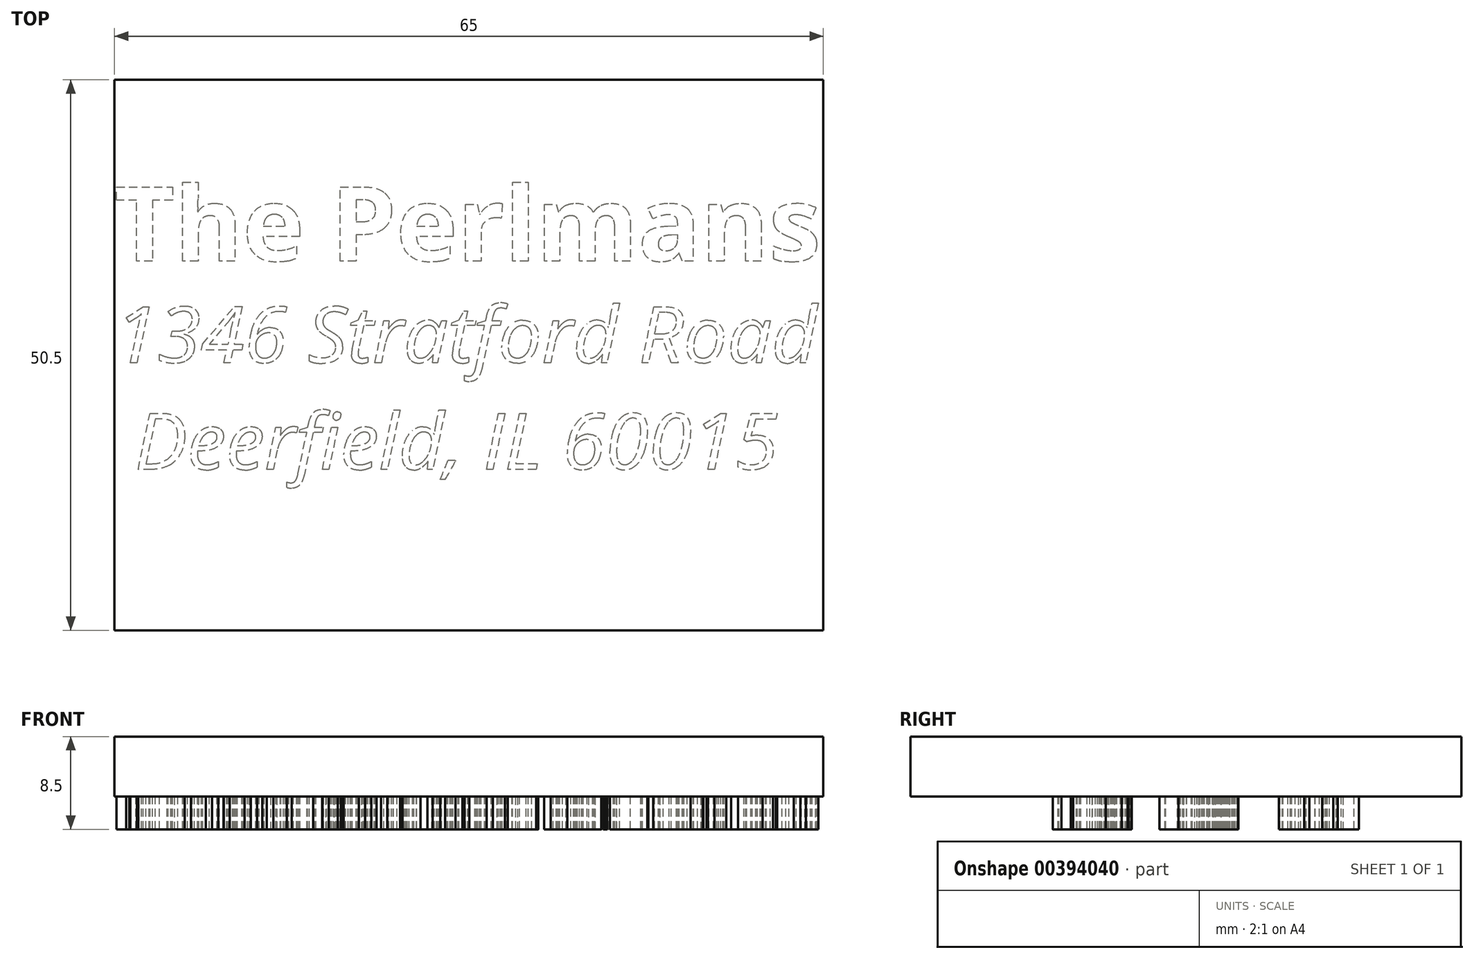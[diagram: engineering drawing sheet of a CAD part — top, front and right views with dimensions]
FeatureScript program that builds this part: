
annotation { "Feature Type Name" : "Feature", "Feature Type Description" : "" }
export const myFeature = defineFeature(function(context is Context, id is Id, definition is map)
    precondition{}
    {
        {
            var Q0;
            Q0=qCreatedBy(makeId("Top.planeOp"),FACE);
            var sketch = newSketch(context, id + "F0", { "sketchPlane" : qUnion([Q0])});
            skLineSegment(sketch, "E0.bottom", {"start": v(-32.5, 25.25) * mm, "end": v(32.5, 25.25) * mm});
            skLineSegment(sketch, "E0.top", {"start": v(-32.5, -25.25) * mm, "end": v(32.5, -25.25) * mm});
            skLineSegment(sketch, "E0.left", {"start": v(-32.5, 25.25) * mm, "end": v(-32.5, -25.25) * mm});
            skLineSegment(sketch, "E0.right", {"start": v(32.5, 25.25) * mm, "end": v(32.5, -25.25) * mm});
            skPoint(sketch, "E0.middle", {"position": v(0, 0) * mm});
            skSolve(sketch);
        }
        {
            var Q0;
            Q0=makeQuery(id+"F0.imprint","IMPRINT",FACE,{"disambiguationData":[TD([[makeQuery(id+"F0.imprint","IMPRINT",EDGE,{"derivedFrom":sQuery(id+"F0.wireOp",EDGE,"E0.bottom")}),-1.0]])]});
            extrude(context, id + "F1", {"entities" : qUnion([Q0]), "depth" : 5.5 * mm});
        }
        {
            var Q0;
            Q0=qCreatedBy(makeId("Top.planeOp"),FACE);
            var sketch = newSketch(context, id + "F2", { "sketchPlane" : qUnion([Q0])});
            skText(sketch, "E1", { "text": "The Perlmans", "fontName": "OpenSans-Bold.ttf"});
            const initialGuessF2  = {"E1": [-0.0325, 0.00863, 1, 0, 0.00685]};
            skSetInitialGuess(sketch, initialGuessF2);
            skSolve(sketch);
        }
        {
            var Q0;
            Q0 = qSketchRegion(id + "F2", true);
            extrude(context, id + "F3", {"entities" : qUnion([Q0]), "operationType" : NewBodyOperationType.ADD, "depth" : -3 * mm});
        }
        {
            var Q0;
            {var subQ0=sQuery(id+"F0.wireOp",EDGE,"E0.left");var subQ1=sQuery(id+"F0.wireOp",EDGE,"E0.top");var subQ2=sQuery(id+"F0.wireOp",EDGE,"E0.right");var subQ3=sQuery(id+"F0.wireOp",EDGE,"E0.bottom");Q0=makeQuery(id+"F3.boolean.opBoolean","SPLIT",FACE,{"disambiguationData":[TD([makeQuery(id+"F1.opExtrude","SWEPT_FACE",FACE,{"disambiguationData":[OSD([subQ3])]})])],"derivedFrom":makeQuery(id+"F1.opExtrude","CAP_FACE",FACE,{"disambiguationData":[OSD([subQ3,subQ1,subQ0,subQ2])],"isStart":false})});}
            var sketch = newSketch(context, id + "F4", { "sketchPlane" : qUnion([Q0])});
            skText(sketch, "E2", { "text": "1346 Stratford Road\n Deerfield, IL 60015", "fontName": "OpenSans-Italic.ttf"});
            const initialGuessF4  = {"E2": [-0.0325, -0.0007, 1, 0, 0.00518]};
            skSetInitialGuess(sketch, initialGuessF4);
            skSolve(sketch);
        }
        {
            var Q0;
            Q0 = qSketchRegion(id + "F4", true);
            extrude(context, id + "F5", {"entities" : qUnion([Q0]), "operationType" : NewBodyOperationType.ADD, "depth" : -8.5 * mm});
        }
    });
